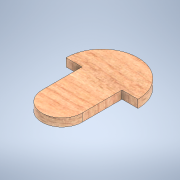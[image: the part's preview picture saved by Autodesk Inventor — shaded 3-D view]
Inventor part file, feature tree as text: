
AUTODESK INVENTOR PART (.ipt)
format: ipt  version: 2022 (Build 260153000, 153)  size: 123,904 bytes
history: native  units: mm
features: other x1, extrude x1, sketch x1
ambient origin geometry x8: Origin, YZ Plane, XZ Plane, XY Plane, X Axis, Y Axis, Z Axis, Center Point
bodies: Body1 (feature_tree)
feature tree (3):
  other  "Sólido1"
  extrude  "Extrusión1"  Depth=50.0mm
  sketch  "Boceto1"  dims[d0=90.0mm d1=50.0mm d2=100.0mm d3=10.0mm d4=0.0mm]
